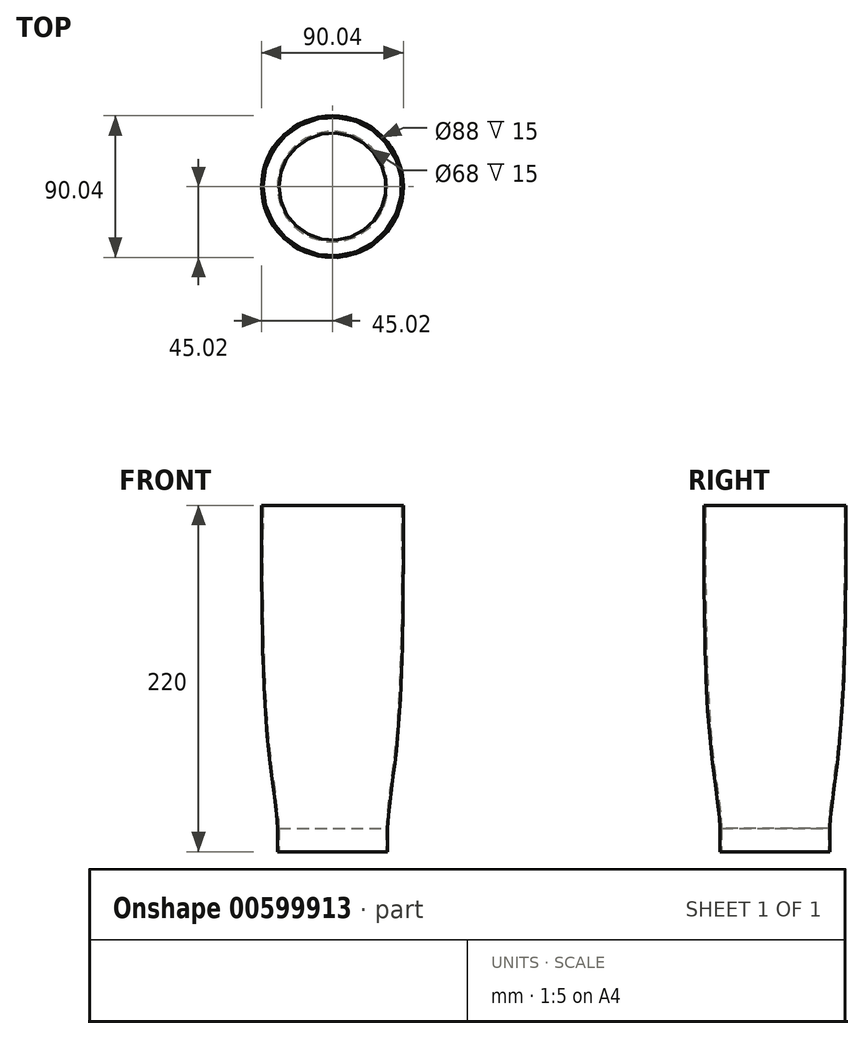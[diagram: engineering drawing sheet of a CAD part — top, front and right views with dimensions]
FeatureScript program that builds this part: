
annotation { "Feature Type Name" : "Feature", "Feature Type Description" : "" }
export const myFeature = defineFeature(function(context is Context, id is Id, definition is map)
    precondition{}
    {
        {
            var Q0;
            Q0=qCreatedBy(makeId("Front.planeOp"),FACE);
            var sketch = newSketch(context, id + "F0", { "sketchPlane" : qUnion([Q0])});
            skLineSegment(sketch, "E0", {"start": v(0, 0) * mm, "end": v(0, 220) * mm, "construction": true});
            skLineSegment(sketch, "E1", {"start": v(0, 0) * mm, "end": v(35, 0) * mm, "construction": true});
            skLineSegment(sketch, "E2", {"start": v(35, 0) * mm, "end": v(35, 80) * mm, "construction": true});
            skLineSegment(sketch, "E3", {"start": v(0, 220) * mm, "end": v(45, 220) * mm, "construction": true});
            skLineSegment(sketch, "E4", {"start": v(45, 220) * mm, "end": v(45, 205) * mm});
            skLineSegment(sketch, "E5", {"start": v(0, 80) * mm, "end": v(42, 80) * mm, "construction": true});
            skLineSegment(sketch, "E6", {"start": v(35, 0) * mm, "end": v(35, 15) * mm});
            skFitSpline(sketch, "E7", {"points": [v(35, 15) * mm, v(42, 80) * mm, v(45, 205) * mm], "startDerivative": vector(0, 89.77) * mm, "endDerivative": vector(0, 81.62) * mm});
            skLineSegment(sketch, "E8.0", {"start": v(34, 0) * mm, "end": v(34, 15) * mm});
            skFitSpline(sketch, "E8.1", {"points": [v(34, 15) * mm, v(34, 18.81) * mm, v(34.6, 25.55) * mm, v(36.1, 36.88) * mm, v(37.42, 46.62) * mm, v(38.59, 55.83) * mm, v(39.5, 63.88) * mm, v(40.16, 70.27) * mm, v(40.77, 77.01) * mm, v(41.32, 84.13) * mm, v(41.8, 91.59) * mm, v(42.37, 101.89) * mm, v(42.93, 115.27) * mm, v(43.41, 131.6) * mm, v(43.73, 147.66) * mm, v(43.98, 168.04) * mm, v(44.04, 190.2) * mm, v(44, 201.6) * mm, v(44, 205) * mm]});
            skLineSegment(sketch, "E8.2", {"start": v(44, 220) * mm, "end": v(44, 205) * mm});
            skLineSegment(sketch, "E9", {"start": v(34, 0) * mm, "end": v(35, 0) * mm});
            skLineSegment(sketch, "E10", {"start": v(44, 220) * mm, "end": v(45, 220) * mm});
            skSolve(sketch);
        }
        {
            var Q0;
            Q0=makeQuery(id+"F0.imprint","IMPRINT",FACE,{"disambiguationData":[TD([[makeQuery(id+"F0.imprint","IMPRINT",EDGE,{"derivedFrom":sQuery(id+"F0.wireOp",EDGE,"E4")}),-1.0]])]});
            var Q1;
            Q1=sQuery(id+"F0.wireOp",EDGE,"E0");
            revolve(context, id + "F1", {"entities" : qUnion([Q0]), "axis" : qUnion([Q1]), "revolveType" : RevolveType.FULL});
        }
    });
